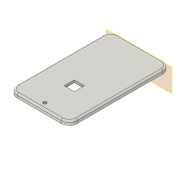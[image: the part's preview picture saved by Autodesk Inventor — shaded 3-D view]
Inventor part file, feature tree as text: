
AUTODESK INVENTOR PART (.ipt)
format: ipt  version: 2019 (Build 230136000, 136)  size: 207,360 bytes
history: native  units: mm
features: extrude x5, sketch x5, projected_geometry x3, fillet x2, plane x1
ambient origin geometry x8: Origin, YZ Plane, XZ Plane, XY Plane, X Axis, Y Axis, Z Axis, Center Point
bodies: Solid1 (feature_tree)
feature tree (16):
  extrude  "Extrusion1"  Depth=74.0mm
  extrude  "Extrusion2"  Depth=3.0mm TaperAngle=0.0deg
  extrude  "Extrusion4"  Depth=2.0mm
  fillet  "Fillet1"  Radius=2.0mm
  plane  "Work Plane1"
  extrude  "Extrusion5"  Depth=8.0mm
  extrude  "Extrusion6"  Depth=12.5mm
  fillet  "Fillet2"  Radius=12.5mm
  sketch  "Sketch1"  dims[d0=125.0mm d1=74.0mm]
  sketch  "Sketch3"  dims[d2=10.0mm d3=3.0mm d4=0.0mm]
  projected_geometry  "Projected Loop1"
  sketch  "Sketch6"  dims[d5=2.0mm d6=2.0mm d7=2.0mm]
  projected_geometry  "Projected Loop6"
  sketch  "Sketch8"  dims[d8=2.0mm d10=8.0mm]
  projected_geometry  "Projected Loop7"
  sketch  "Sketch10"  dims[d11=2.0mm d12=0.0mm d28=12.5mm d29=12.5mm d31=10.75mm d32=0.0mm d33=2.0mm d34=7.0mm d35=9.0mm d36=10.0mm d37=10.0mm d38=3.0mm d39=2.0mm d40=0.0mm d41=35.0mm d42=5.0mm d43=3.5mm d44=5.75mm d45=0.0mm d46=0.25mm]
